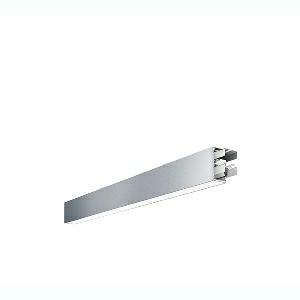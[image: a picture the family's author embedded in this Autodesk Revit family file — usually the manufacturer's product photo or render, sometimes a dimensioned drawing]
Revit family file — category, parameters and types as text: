
# Revit family: dotoo_line_-_dla_2000_840_d_sta_00807955_3b42
name_source: partatom
category: Lighting Fixtures
units: mm (PartAtom-declared; Revit-internal decimal feet)

## family parameters
Cut with Voids When Loaded = No
Host = Face
Light Source = No
Part Type = Normal
Room Calculation Point = No
Round Connector Dimension = Use Diameter
Shared = No

## types (1)
- DOTOO.line - DLA 2000/840/D STA (1 x LED, 1700 lm, 4000K)
    Apparent Load = 16 VA
    Approval mark = CE
    CIE Flux Codes = 67 91 98 100 100
    Color Rendering = 80-89
    Color Temperature = 4000K
    Control Gear = Electronic ballast
    Default Elevation = 1800 mm
    Description = DLA 2000/840/D|Surface-mounted luminaire.|light source: LED|work equipment: Adjustable electronic ballast, digital DALI|connected load: 220-240 V, 50/60 Hz|Power consumption: approx. 16 W|luminous flux: 1700 lm|luminous efficacy: 106 lm/W|light distribution: Direct|colour temperature: Cold white, ca. 4000 K|class of protection: I|technology: Continuously dimmable|mains lead: Connector|glare control: Prism aperture|special features: DALI Load 1x, TouchDIM - dimming via standard switch, Through-wired, up to 18 m on one mains connection, Flicker-free, Suitable as emergency lighting, Start luminaire with mains connection, Maintenance-friendly due to easily accessible ballasts|
    Frequency = 50 Hz
    Height = 110 mm
    Lamp = 1 x LED
    Lamp Light Flux = 1700 lm
    Lamp count = 1
    Length = 1408 mm
    Luminous efficacy = 106 lm/W
    Manufacturer = Waldmann
    ModVariant = No
    Model = 00807955
    Mounting Place = Ceiling
    Mounting Type = Surface mounted
    Number of Poles = 1
    OnlyDefault = Yes
    Power Factor = 1
    Product Name = DOTOO.line - DLA 2000/840/D STA
    Product group = Ceiling mounted luminaire
    ProductGroupID = 3
    Protection Class = Protection class I
    Protection Degree = IP 40
    RLX_Detail_Level = 1
    RLX_Emergency_Light_Flux = 0 lm
    RLX_Emergency_Type = 0
    RLX_Emergency_Type_DB = No
    RlxData = <blob elided: 18365 chars, md5=883b393c>
    Socket = socket
    Standby Power = 0 W
    System Light Flux = 1700 lm
    System Power = 16 W
    Type Comments = Product without accessories
    Type Image = 114372000-00807949.jpg
    URL = http://relux.com
    VarID = ---
    Voltage = 230 V
    Voltage Range = 220-240 V
    Weight = 0.00 kg
    Width = 60 mm  [stored 0.19685 ft]

note: [stored X ft] marks values corroborated as IEEE doubles in the binary element streams (Revit-internal decimal feet)

## geometry (parser evidence)
native form markers: Blend x4, Sweep x12
no freeform markers — native parametric forms only
